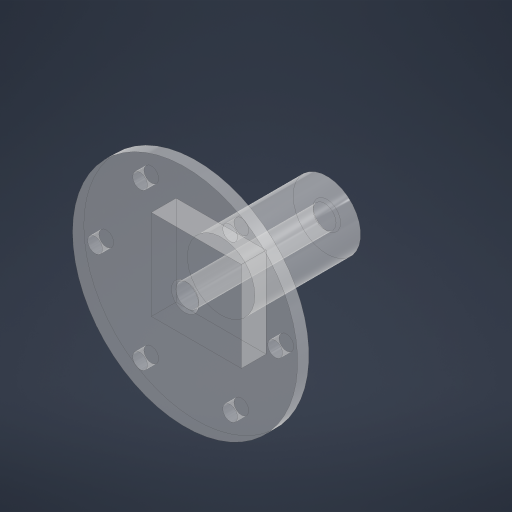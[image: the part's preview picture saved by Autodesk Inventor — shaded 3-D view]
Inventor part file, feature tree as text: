
AUTODESK INVENTOR PART (.ipt)
format: ipt  version: 2024.1 (Build 281209000, 209)  size: 268,288 bytes
history: native  units: in
note: dims shown in document units (in); Inventor stores cm internally (conversion verified against a paired STEP export)
features: extrude x6, other x5, sketch x4, reference x3, plane x1, chamfer x1
ambient origin geometry x8: Origin, YZ Plane, XZ Plane, XY Plane, X Axis, Y Axis, Z Axis, Center Point
bodies: Solid1 (feature_tree)
feature tree (20):
  extrude  "Extrusion1"  Depth=0.003in
  plane  "Work Plane1"
  sketch  "Sketch2"  dims[d2=0.5906in d3=5.0787in d4=0.0in d5=0.0in d6=5.4134in]
  extrude  "Extrusion2"  Depth=5.4134in
  extrude  "Extrusion3"  Depth=1.0in
  extrude  "Extrusion4"  Depth=0.125in
  extrude  "Extrusion5"  Depth=0.125in
  extrude  "Extrusion6"  Depth=1.0in
  chamfer  "Chamfer2"  Distance=2.3622in Angle=360.0deg
  sketch  "Sketch1"  dims[d0=0.002in d1=0.003in]
  reference  "Reference1"
  reference  "Reference2"
  sketch  "Sketch3"  dims[d7=21.6535in d8=1.0in]
  sketch  "Sketch4"  dims[d9=2.5in d10=24.0in d11=0.1654in d12=1.0in d13=2.3622in d15=360.0deg d17=1.0in d18=1.0in d19=0.75in d20=1.5748in d21=0.0in d22=0.4in d23=0.0in d24=0.125in d25=0.0in d29=0.005in d30=0.0in d31=0.0in d32=0.002in d33=1.5748in d34=0.0in d35=0.025in d36=0.125in d37=45.0deg]
  reference  "Reference3"
  other  "Assembly1"
  other  "BallBearing_8x22x7mm:1"
  other  "AcrylicRod:1"
  other  "<userpath>\Documents\School\FallCAD\Trebuchet\Trebuchet.iam"
  other  "Trebuchet.iam"
